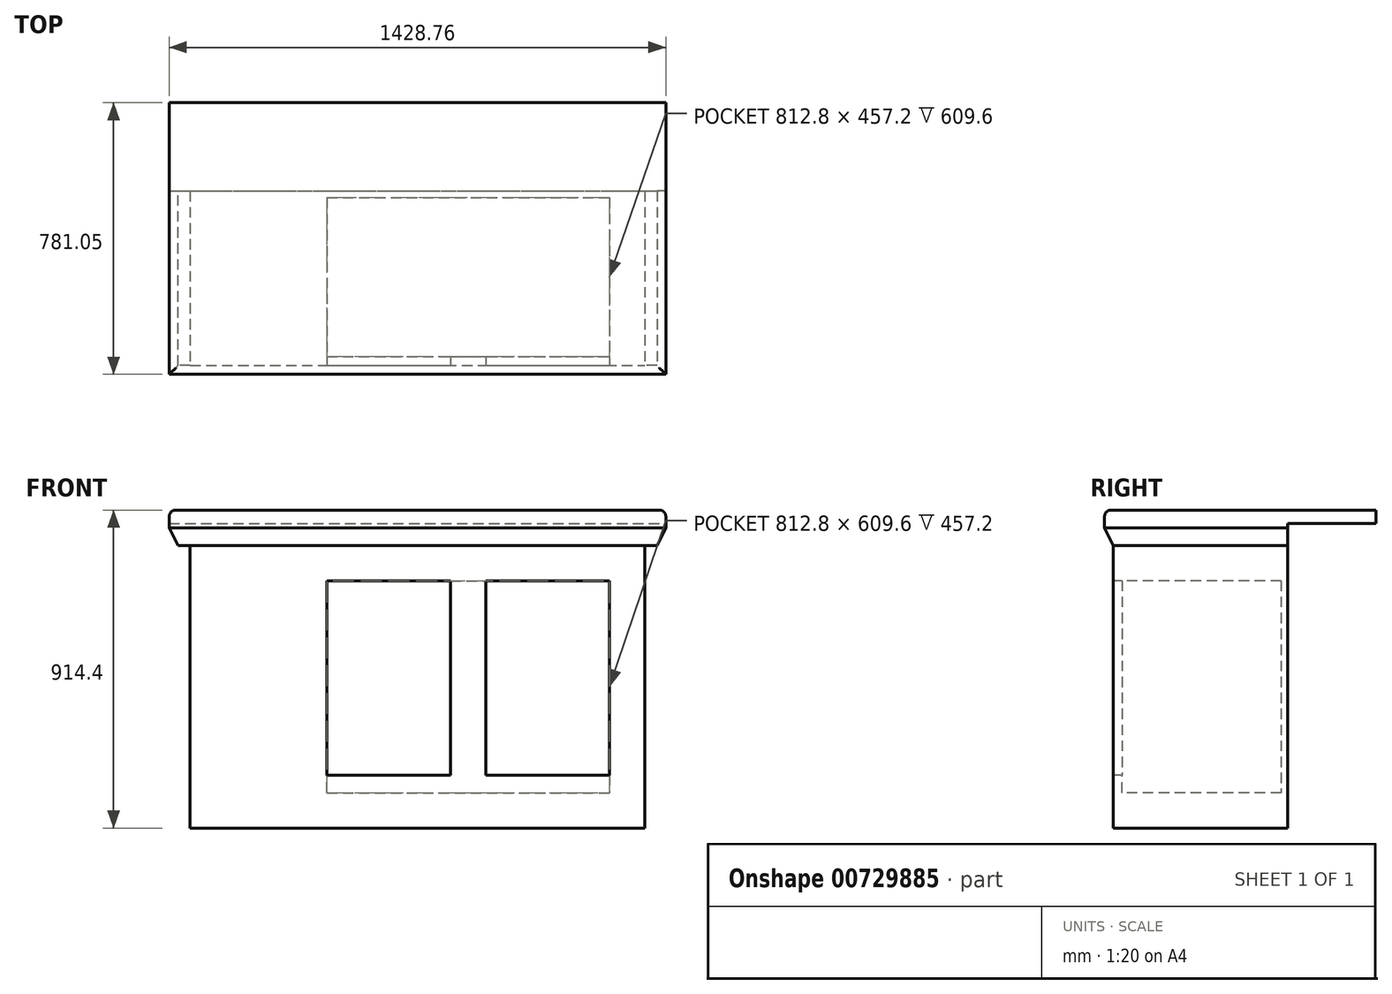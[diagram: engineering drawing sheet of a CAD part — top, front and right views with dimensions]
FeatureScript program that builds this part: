
annotation { "Feature Type Name" : "Feature", "Feature Type Description" : "" }
export const myFeature = defineFeature(function(context is Context, id is Id, definition is map)
    precondition{}
    {
        {
            var Q0;
            Q0=qCreatedBy(makeId("Top.planeOp"),FACE);
            var sketch = newSketch(context, id + "F0", { "sketchPlane" : qUnion([Q0])});
            skLineSegment(sketch, "E0.bottom", {"start": v(-1308.1, 501.65) * mm, "end": v(0, 501.65) * mm});
            skLineSegment(sketch, "E0.top", {"start": v(-1308.1, 0) * mm, "end": v(0, 0) * mm});
            skLineSegment(sketch, "E0.left", {"start": v(-1308.1, 501.65) * mm, "end": v(-1308.1, 0) * mm});
            skLineSegment(sketch, "E0.right", {"start": v(0, 501.65) * mm, "end": v(0, 0) * mm});
            skSolve(sketch);
        }
        {
            var Q0;
            Q0=makeQuery(id+"F0.imprint","IMPRINT",FACE,{"disambiguationData":[TD([[makeQuery(id+"F0.imprint","IMPRINT",EDGE,{"derivedFrom":sQuery(id+"F0.wireOp",EDGE,"E0.bottom")}),-1.0]])]});
            extrude(context, id + "F1", {"entities" : qUnion([Q0]), "depth" : 812.8 * mm, "offsetDistance" : 25.4 * mm});
        }
        {
            var Q0;
            Q0=makeQuery(id+"F1.opExtrude","CAP_FACE",FACE,{"disambiguationData":[OSD([sQuery(id+"F0.wireOp",EDGE,"E0.bottom"),sQuery(id+"F0.wireOp",EDGE,"E0.top"),sQuery(id+"F0.wireOp",EDGE,"E0.left"),sQuery(id+"F0.wireOp",EDGE,"E0.right")])],"isStart":false});
            var sketch = newSketch(context, id + "F2", { "sketchPlane" : qUnion([Q0])});
            skLineSegment(sketch, "E1.bottom", {"start": v(-1368.43, 501.65) * mm, "end": v(60.32, 501.65) * mm});
            skLineSegment(sketch, "E1.top", {"start": v(-1368.43, -25.4) * mm, "end": v(60.32, -25.4) * mm});
            skLineSegment(sketch, "E1.left", {"start": v(-1368.43, 501.65) * mm, "end": v(-1368.43, -25.4) * mm});
            skLineSegment(sketch, "E1.right", {"start": v(60.32, 501.65) * mm, "end": v(60.33, -25.4) * mm});
            skSolve(sketch);
        }
        {
            var Q0;
            Q0 = qSketchRegion(id + "F2", true);
            extrude(context, id + "F3", {"entities" : qUnion([Q0]), "operationType" : NewBodyOperationType.ADD, "depth" : 63.5 * mm, "offsetDistance" : 25.4 * mm});
        }
        {
            var Q0;
            Q0=makeQuery(id+"F3.opExtrude","CAP_EDGE",EDGE,{"disambiguationData":[OSD([sQuery(id+"F2.wireOp",EDGE,"E1.left")])],"isStart":true});
            var Q1;
            Q1=makeQuery(id+"F3.opExtrude","CAP_EDGE",EDGE,{"disambiguationData":[OSD([sQuery(id+"F2.wireOp",EDGE,"E1.top")])],"isStart":true});
            var Q2;
            Q2=makeQuery(id+"F3.opExtrude","CAP_EDGE",EDGE,{"disambiguationData":[OSD([sQuery(id+"F2.wireOp",EDGE,"E1.right")])],"isStart":true});
            chamfer(context, id + "F4", {"entities" : qUnion([Q0, Q1, Q2]), "chamferType" : ChamferType.TWO_OFFSETS, "width1" : 50.8 * mm, "oppositeDirection" : false, "width2" : 25.4 * mm, "tangentPropagation" : true});
        }
        {
            var Q0;
            Q0=makeQuery(id+"F3.opExtrude","CAP_FACE",FACE,{"disambiguationData":[OSD([sQuery(id+"F2.wireOp",EDGE,"E1.bottom"),sQuery(id+"F2.wireOp",EDGE,"E1.top"),sQuery(id+"F2.wireOp",EDGE,"E1.left"),sQuery(id+"F2.wireOp",EDGE,"E1.right")])],"isStart":false});
            var sketch = newSketch(context, id + "F5", { "sketchPlane" : qUnion([Q0])});
            skLineSegment(sketch, "E2.bottom", {"start": v(60.33, -25.4) * mm, "end": v(-1368.43, -25.4) * mm});
            skLineSegment(sketch, "E2.top", {"start": v(60.32, 755.65) * mm, "end": v(-1368.43, 755.65) * mm});
            skLineSegment(sketch, "E2.left", {"start": v(60.33, -25.4) * mm, "end": v(60.33, 755.65) * mm});
            skLineSegment(sketch, "E2.right", {"start": v(-1368.43, -25.4) * mm, "end": v(-1368.43, 755.65) * mm});
            skSolve(sketch);
        }
        {
            var Q0;
            {var subQ0=sQuery(id+"F5.wireOp",EDGE,"E2.bottom");Q0=makeQuery(id+"F5.imprint","IMPRINT",FACE,{"disambiguationData":[TD([[makeQuery(id+"F5.imprint","IMPRINT",EDGE,{"derivedFrom":subQ0}),1.0]])]});}
            var Q1;
            {var subQ0=sQuery(id+"F5.wireOp",EDGE,"E2.top");Q1=makeQuery(id+"F5.imprint","IMPRINT",FACE,{"disambiguationData":[TD([[makeQuery(id+"F5.imprint","IMPRINT",EDGE,{"derivedFrom":subQ0}),1.0]])]});}
            extrude(context, id + "F6", {"entities" : qUnion([Q0, Q1]), "operationType" : NewBodyOperationType.ADD, "depth" : 38.1 * mm, "offsetDistance" : 25.4 * mm});
        }
        {
            var Q0;
            Q0=makeQuery(id+"F6.opExtrude","CAP_EDGE",EDGE,{"disambiguationData":[OSD([sQuery(id+"F5.wireOp",EDGE,"E2.right")])],"isStart":false});
            var Q1;
            Q1=makeQuery(id+"F6.opExtrude","CAP_EDGE",EDGE,{"disambiguationData":[OSD([sQuery(id+"F5.wireOp",EDGE,"E2.bottom")])],"isStart":false});
            var Q2;
            Q2=makeQuery(id+"F6.opExtrude","CAP_EDGE",EDGE,{"disambiguationData":[OSD([sQuery(id+"F5.wireOp",EDGE,"E2.left")])],"isStart":false});
            fillet(context, id + "F7", {"entities" : qUnion([Q0, Q1, Q2]), "radius" : 19.05 * mm, "tangentPropagation" : true, "allowEdgeOverflow" : false});
        }
        {
            var Q0;
            Q0=makeQuery(id+"F1.opExtrude","SWEPT_FACE",FACE,{"disambiguationData":[OSD([sQuery(id+"F0.wireOp",EDGE,"E0.top")])]});
            var sketch = newSketch(context, id + "F8", { "sketchPlane" : qUnion([Q0])});
            skLineSegment(sketch, "E3.bottom", {"start": v(-457.2, 711.2) * mm, "end": v(-101.6, 711.2) * mm});
            skLineSegment(sketch, "E3.top", {"start": v(-457.2, 152.4) * mm, "end": v(-101.6, 152.4) * mm});
            skLineSegment(sketch, "E3.left", {"start": v(-457.2, 711.2) * mm, "end": v(-457.2, 152.4) * mm});
            skLineSegment(sketch, "E3.right", {"start": v(-101.6, 711.2) * mm, "end": v(-101.6, 152.4) * mm});
            skLineSegment(sketch, "E4.bottom", {"start": v(-914.4, 711.2) * mm, "end": v(-558.8, 711.2) * mm});
            skLineSegment(sketch, "E4.top", {"start": v(-914.4, 152.4) * mm, "end": v(-558.8, 152.4) * mm});
            skLineSegment(sketch, "E4.left", {"start": v(-914.4, 711.2) * mm, "end": v(-914.4, 152.4) * mm});
            skLineSegment(sketch, "E4.right", {"start": v(-558.8, 711.2) * mm, "end": v(-558.8, 152.4) * mm});
            skSolve(sketch);
        }
        {
            var Q0;
            Q0 = qSketchRegion(id + "F8", true);
            extrude(context, id + "F9", {"entities" : qUnion([Q0]), "operationType" : NewBodyOperationType.REMOVE, "oppositeDirection" : true, "depth" : 482.6 * mm, "offsetDistance" : 25.4 * mm});
        }
        {
            var Q0;
            Q0=makeQuery(id+"F9.boolean.opBoolean","COPY",FACE,{"derivedFrom":makeQuery(id+"F9.opExtrude","SWEPT_FACE",FACE,{"disambiguationData":[OSD([sQuery(id+"F8.wireOp",EDGE,"E3.left")])]})});
            var sketch = newSketch(context, id + "F10", { "sketchPlane" : qUnion([Q0])});
            skLineSegment(sketch, "E5.bottom", {"start": v(25.4, 711.2) * mm, "end": v(482.6, 711.2) * mm});
            skLineSegment(sketch, "E5.top", {"start": v(25.4, 152.4) * mm, "end": v(482.6, 152.4) * mm});
            skLineSegment(sketch, "E5.left", {"start": v(25.4, 711.2) * mm, "end": v(25.4, 152.4) * mm});
            skLineSegment(sketch, "E5.right", {"start": v(482.6, 711.2) * mm, "end": v(482.6, 152.4) * mm});
            skSolve(sketch);
        }
        {
            var Q0;
            Q0=makeQuery(id+"F10.imprint","IMPRINT",FACE,{"disambiguationData":[TD([[makeQuery(id+"F10.imprint","IMPRINT",EDGE,{"derivedFrom":sQuery(id+"F10.wireOp",EDGE,"E5.bottom")}),1.0]])]});
            extrude(context, id + "F11", {"entities" : qUnion([Q0]), "operationType" : NewBodyOperationType.REMOVE, "oppositeDirection" : true, "depth" : 152.4 * mm, "offsetDistance" : 25.4 * mm});
        }
        {
            var Q0;
            Q0=makeQuery(id+"F11.boolean.opBoolean","MERGE",FACE,{"derivedFrom":[makeQuery(id+"F9.boolean.opBoolean","COPY",FACE,{"derivedFrom":makeQuery(id+"F9.opExtrude","SWEPT_FACE",FACE,{"disambiguationData":[OSD([sQuery(id+"F8.wireOp",EDGE,"E3.top")])]})}),makeQuery(id+"F9.boolean.opBoolean","COPY",FACE,{"derivedFrom":makeQuery(id+"F9.opExtrude","SWEPT_FACE",FACE,{"disambiguationData":[OSD([sQuery(id+"F8.wireOp",EDGE,"E4.top")])]})}),makeQuery(id+"F11.opExtrude","SWEPT_FACE",FACE,{"disambiguationData":[OSD([sQuery(id+"F10.wireOp",EDGE,"E5.top")])]})]});
            var sketch = newSketch(context, id + "F12", { "sketchPlane" : qUnion([Q0])});
            skLineSegment(sketch, "E6.bottom", {"start": v(-914.4, 482.6) * mm, "end": v(-101.6, 482.6) * mm});
            skLineSegment(sketch, "E6.top", {"start": v(-914.4, 25.4) * mm, "end": v(-101.6, 25.4) * mm});
            skLineSegment(sketch, "E6.left", {"start": v(-914.4, 482.6) * mm, "end": v(-914.4, 25.4) * mm});
            skLineSegment(sketch, "E6.right", {"start": v(-101.6, 482.6) * mm, "end": v(-101.6, 25.4) * mm});
            skSolve(sketch);
        }
        {
            var Q0;
            Q0=makeQuery(id+"F12.imprint","IMPRINT",FACE,{"disambiguationData":[TD([[makeQuery(id+"F12.imprint","IMPRINT",EDGE,{"derivedFrom":sQuery(id+"F12.wireOp",EDGE,"E6.bottom")}),-1.0]])]});
            extrude(context, id + "F13", {"entities" : qUnion([Q0]), "operationType" : NewBodyOperationType.REMOVE, "oppositeDirection" : true, "depth" : 50.8 * mm, "offsetDistance" : 25.4 * mm});
        }
    });
